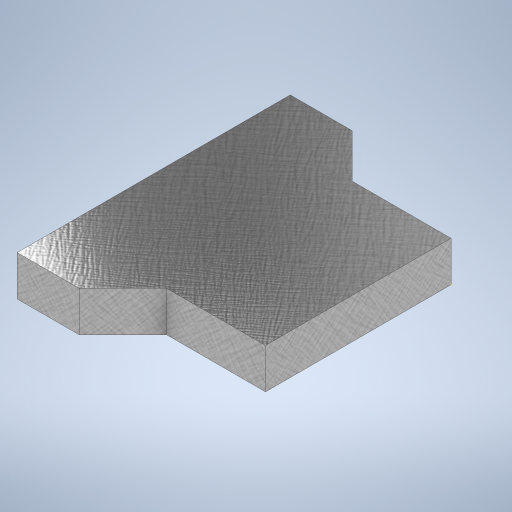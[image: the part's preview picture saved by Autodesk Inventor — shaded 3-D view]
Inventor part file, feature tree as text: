
AUTODESK INVENTOR PART (.ipt)
format: ipt  version: 2024 (Build 280153000, 153)  size: 307,200 bytes
history: native  units: mm
features: sketch x2, extrude x1
ambient origin geometry x8: Origin, YZ Plane, XZ Plane, XY Plane, X Axis, Y Axis, Z Axis, Center Point
bodies: Solid1 (feature_tree)
feature tree (3):
  sketch  "Sketch1"  dims[d2=15.0mm d3=8.0mm]
  extrude  "Extrusion1"  Depth=8.0mm
  sketch  "Sketch2"  dims[d4=5.0mm d5=45.0deg d6=5.0mm d7=3.25mm d8=0.0mm]
